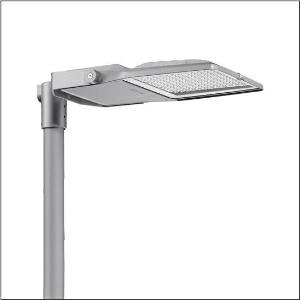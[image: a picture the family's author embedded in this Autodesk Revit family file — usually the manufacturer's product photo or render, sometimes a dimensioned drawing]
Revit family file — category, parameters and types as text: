
# Revit family: floodlight_fl_21_iq_midi___pl52_5xa7782e2d3a_7997
name_source: partatom
category: Lighting Fixtures
units: mm (PartAtom-declared; Revit-internal decimal feet)

## family parameters
Cut with Voids When Loaded = No
Host = Face
Light Source = No
Part Type = Normal
Room Calculation Point = No
Round Connector Dimension = Use Diameter
Shared = No

## types (1)
- --- (1 x LED, 26850 lm, 208.1 W, 3000K)
    Apparent Load = 208 VA
    CIE Flux Codes = 26 60 98 100 100
    Color Rendering = 70
    Color Temperature = 3000K
    Default Elevation = 1800 mm
    Description = Floodlight FL 21 iQ midi, floodlight, primary light control with lens, of PMMA, primary optical cover: protective disc, of toughened safety glass, transparent, light distribution: PL52, light emission: direct distribution, installation type: surface-mounted, LED, High Power LED, rated luminous flux: 26.850lm, luminous efficacy: 129lm/W, light colour: 730, colour temperature: 3000K, control gear: ECG iQ, control: optimised constant luminous flux control (CLO 2.0), Desk-Remote (wireless, voltage-free reading and setting of iQ features in the workshop via application-optimized NFC function/RFID function), Smart-Wire, Night-Set, Temp-Guard, Auto-Match, Street-Remote, with terminal, 6-pole, mains connection: 220..240V, AC, 50/60Hz, start of lifetime: 208W, end of service life: 227W, reduction: 90W, luminaire housing, of diecast aluminium, powder-coated, Siteco® metallic grey (DB 702S), corrosivity category C5 mid according to DIN EN ISO 12944, sealing non-destructively replaceable, please order mast flange separately, mast bracket, of steel, galvanised, powder-coated, Siteco® metallic grey (DB 702S), protection rating (complete): IP66, insulation class (complete): insulation class II (safety insulation), certification: CE, protection symbol: D, impact resistance: IK08, permissible operating ambient temperature: -40..+40°C, permissible operating ambient temperature for outdoor applications: -40..+50°C, standard: DIN EN 12944, LABS conformity tested according to VDMA 24364:2018-05, packaging unit: 1 piece

Light Distribution: PL52
    Height = 76 mm
    Lamp = 1 x LED
    Lamp Light Flux = 26850 lm
    Lamp Power = 208.1 W
    Lamp count = 1
    Length = 657 mm
    Luminous efficacy = 129 lm/W
    Manufacturer = Siteco
    ModVariant = No
    Model = 5XA7782E2D3A
    Number of Poles = 1
    OnlyDefault = Yes
    Power Factor = 1
    Product Name = Floodlight FL 21 iQ midi | PL52
    Product group = floodlight | pylon annexe
    ProductGroupID = 6200
    Protection Class = Protection class II
    Protection Degree = IP 66
    RLX_Detail_Level = 1
    RLX_Emergency_Light_Flux = 0 lm
    RLX_Emergency_Type = 0
    RLX_Emergency_Type_DB = No
    RlxData = <blob elided: 153805 chars, md5=c58730f2>
    Socket = socket
    Standby Power = 0 W
    System Light Flux = 26850 lm
    System Power = 208 W
    Type Comments = factory setting: luminous flux: 100 % | dim-lin: 254 | 710 mA
    Type Image = l_1007123.jpg
    URL = http://relux.com
    VarID = @adj_054371
    Voltage = 0 V
    Weight = 0.00 kg
    Width = 442 mm

## geometry (parser evidence)
native form markers: Blend x4, Sweep x14
no freeform markers — native parametric forms only
